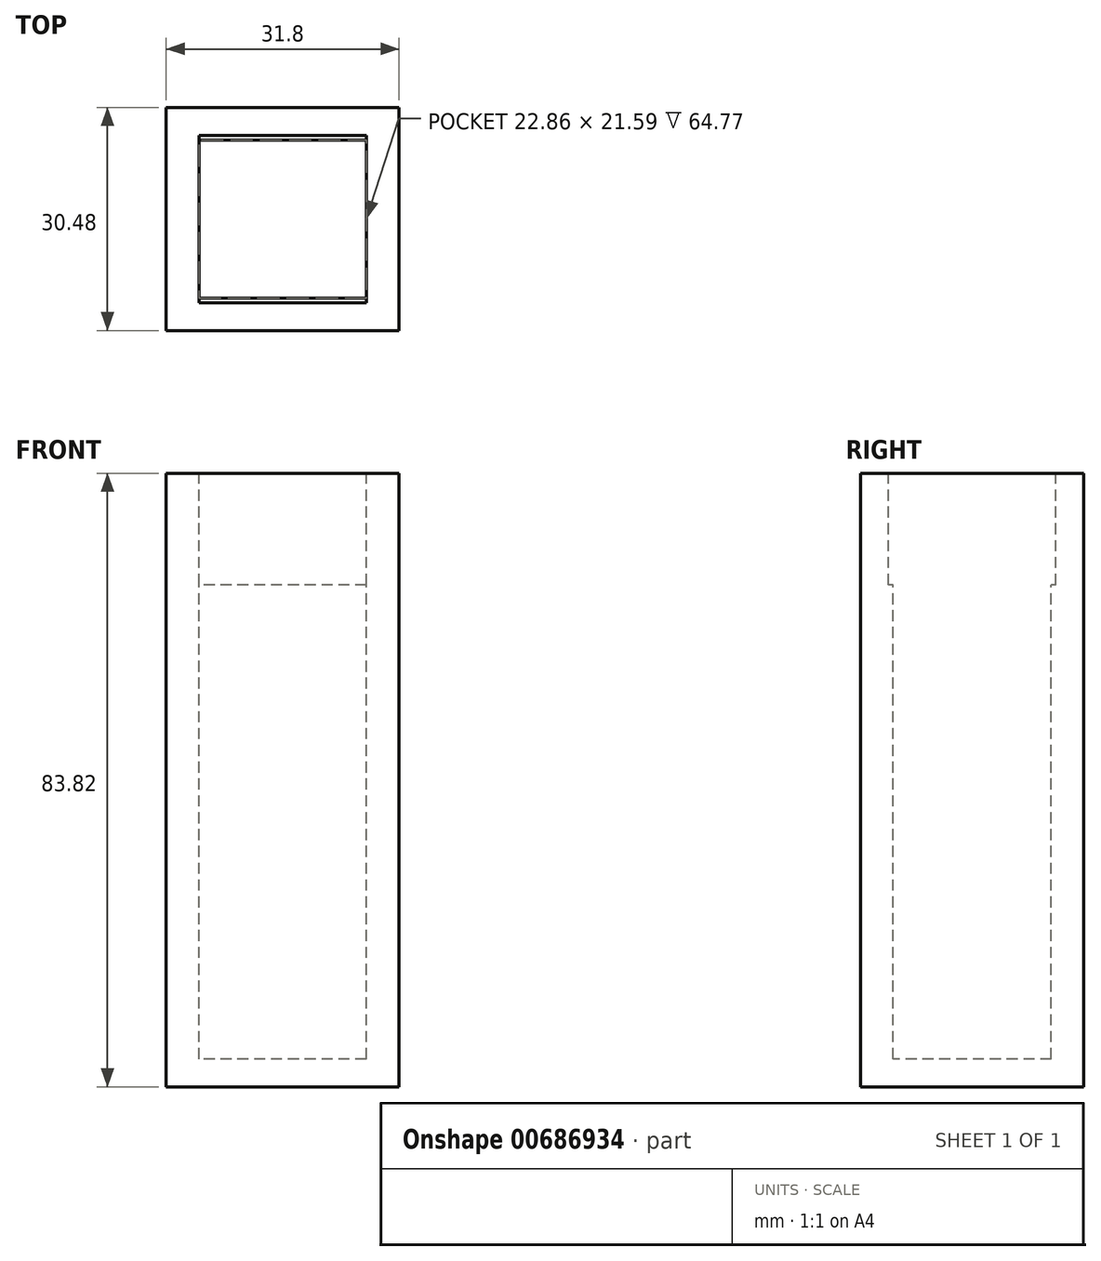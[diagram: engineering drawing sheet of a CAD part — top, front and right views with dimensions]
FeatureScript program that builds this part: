
annotation { "Feature Type Name" : "Feature", "Feature Type Description" : "" }
export const myFeature = defineFeature(function(context is Context, id is Id, definition is map)
    precondition{}
    {
        {
            var Q0;
            Q0=qCreatedBy(makeId("Top.planeOp"),FACE);
            var sketch = newSketch(context, id + "F0", { "sketchPlane" : qUnion([Q0])});
            skLineSegment(sketch, "E0.bottom", {"start": v(15.9, 15.24) * mm, "end": v(-15.9, 15.24) * mm});
            skLineSegment(sketch, "E0.top", {"start": v(15.9, -15.24) * mm, "end": v(-15.9, -15.24) * mm});
            skLineSegment(sketch, "E0.left", {"start": v(15.9, 15.24) * mm, "end": v(15.9, -15.24) * mm});
            skLineSegment(sketch, "E0.right", {"start": v(-15.9, 15.24) * mm, "end": v(-15.9, -15.24) * mm});
            skPoint(sketch, "E0.middle", {"position": v(0, 0) * mm});
            skSolve(sketch);
        }
        {
            var Q0;
            Q0 = qSketchRegion(id + "F0", true);
            extrude(context, id + "F1", {"entities" : qUnion([Q0]), "depth" : 83.82 * mm, "offsetDistance" : 25.4 * mm});
        }
        {
            var Q0;
            Q0=makeQuery(id+"F1.opExtrude","CAP_FACE",FACE,{"disambiguationData":[OSD([sQuery(id+"F0.wireOp",EDGE,"E0.bottom"),sQuery(id+"F0.wireOp",EDGE,"E0.top"),sQuery(id+"F0.wireOp",EDGE,"E0.left"),sQuery(id+"F0.wireOp",EDGE,"E0.right")])],"isStart":false});
            var sketch = newSketch(context, id + "F2", { "sketchPlane" : qUnion([Q0])});
            skLineSegment(sketch, "E1.bottom", {"start": v(11.43, 11.43) * mm, "end": v(-11.43, 11.43) * mm});
            skLineSegment(sketch, "E1.top", {"start": v(11.43, -11.43) * mm, "end": v(-11.43, -11.43) * mm});
            skLineSegment(sketch, "E1.left", {"start": v(11.43, 11.43) * mm, "end": v(11.43, -11.43) * mm});
            skLineSegment(sketch, "E1.right", {"start": v(-11.43, 11.43) * mm, "end": v(-11.43, -11.43) * mm});
            skPoint(sketch, "E1.middle", {"position": v(0, 0) * mm});
            skSolve(sketch);
        }
        {
            var Q0;
            Q0 = qSketchRegion(id + "F2", true);
            extrude(context, id + "F3", {"entities" : qUnion([Q0]), "operationType" : NewBodyOperationType.REMOVE, "oppositeDirection" : true, "depth" : 15.24 * mm, "offsetDistance" : 25.4 * mm});
        }
        {
            var Q0;
            Q0=makeQuery(id+"F3.boolean.opBoolean","COPY",FACE,{"derivedFrom":makeQuery(id+"F3.opExtrude","CAP_FACE",FACE,{"disambiguationData":[OSD([sQuery(id+"F2.wireOp",EDGE,"E1.bottom"),sQuery(id+"F2.wireOp",EDGE,"E1.top"),sQuery(id+"F2.wireOp",EDGE,"E1.left"),sQuery(id+"F2.wireOp",EDGE,"E1.right")])],"isStart":false})});
            var sketch = newSketch(context, id + "F4", { "sketchPlane" : qUnion([Q0])});
            skLineSegment(sketch, "E2.bottom", {"start": v(11.43, -10.8) * mm, "end": v(-11.43, -10.8) * mm});
            skLineSegment(sketch, "E2.top", {"start": v(11.43, 10.8) * mm, "end": v(-11.43, 10.8) * mm});
            skLineSegment(sketch, "E2.left", {"start": v(11.43, -10.8) * mm, "end": v(11.43, 10.8) * mm});
            skLineSegment(sketch, "E2.right", {"start": v(-11.43, -10.8) * mm, "end": v(-11.43, 10.8) * mm});
            skPoint(sketch, "E2.middle", {"position": v(0, 0) * mm});
            skSolve(sketch);
        }
        {
            var Q0;
            Q0 = qSketchRegion(id + "F4", true);
            extrude(context, id + "F5", {"entities" : qUnion([Q0]), "operationType" : NewBodyOperationType.REMOVE, "oppositeDirection" : true, "depth" : 64.77 * mm, "offsetDistance" : 25.4 * mm});
        }
    });
